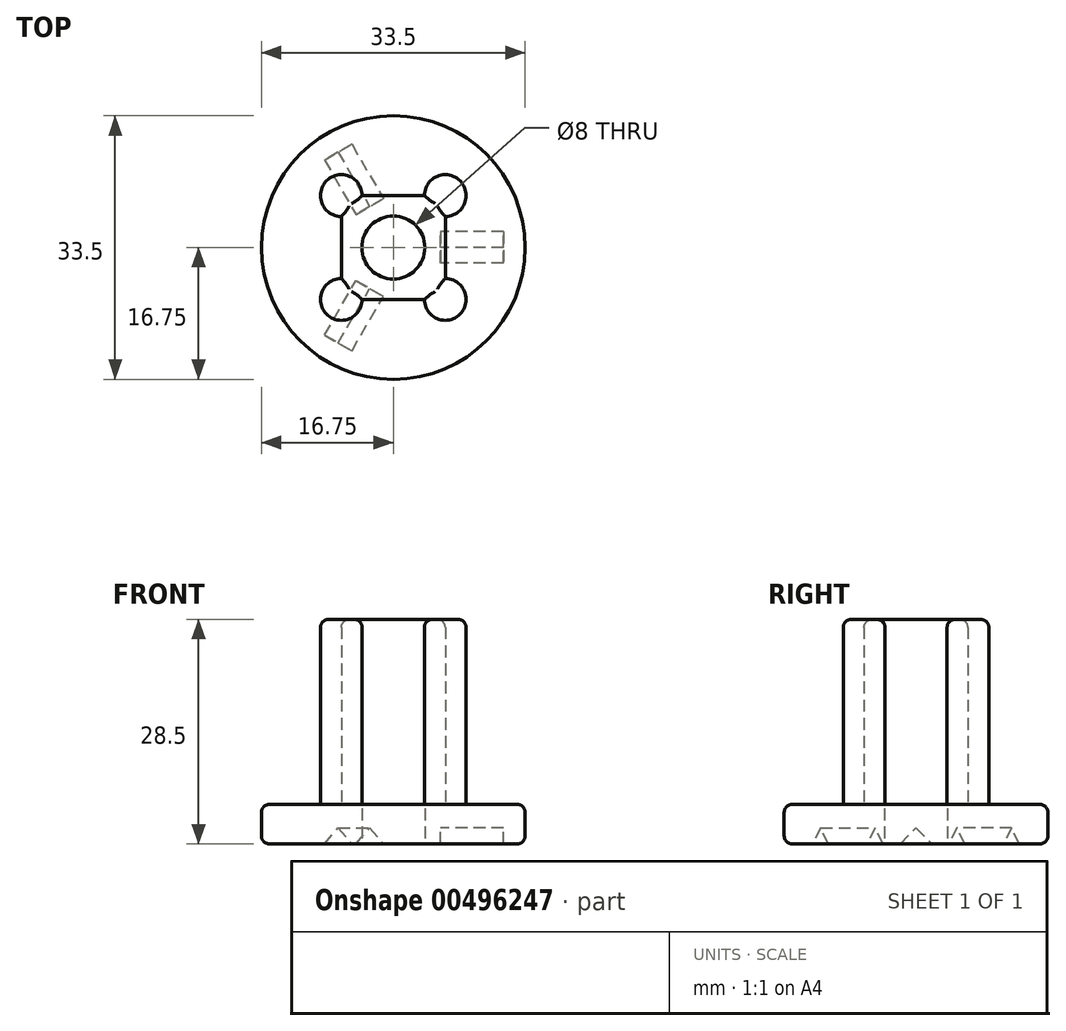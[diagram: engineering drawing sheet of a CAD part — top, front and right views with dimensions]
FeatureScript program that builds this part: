
annotation { "Feature Type Name" : "Feature", "Feature Type Description" : "" }
export const myFeature = defineFeature(function(context is Context, id is Id, definition is map)
    precondition{}
    {
        {
            var Q0;
            Q0=qCreatedBy(makeId("Top.planeOp"),FACE);
            var sketch = newSketch(context, id + "F0", { "sketchPlane" : qUnion([Q0])});
            skCircle(sketch, "E0", {"center": v(0, 0) * mm, "radius": 16.75 * mm});
            skSolve(sketch);
        }
        {
            var Q0;
            Q0=makeQuery(id+"F0.imprint","IMPRINT",FACE,{"disambiguationData":[TD([[makeQuery(id+"F0.imprint","IMPRINT",EDGE,{"derivedFrom":sQuery(id+"F0.wireOp",EDGE,"E0")}),1.0]])]});
            extrude(context, id + "F1", {"entities" : qUnion([Q0]), "depth" : 5 * mm});
        }
        {
            var Q0;
            Q0=makeQuery(id+"F1.opExtrude","CAP_FACE",FACE,{"disambiguationData":[OSD([sQuery(id+"F0.wireOp",EDGE,"E0")])],"isStart":false});
            var sketch = newSketch(context, id + "F2", { "sketchPlane" : qUnion([Q0])});
            skLineSegment(sketch, "E1.bottom", {"start": v(-3.95, 6.6) * mm, "end": v(3.95, 6.6) * mm});
            skLineSegment(sketch, "E1.top", {"start": v(-3.95, -6.6) * mm, "end": v(3.95, -6.6) * mm});
            skLineSegment(sketch, "E1.left", {"start": v(-6.6, 3.95) * mm, "end": v(-6.6, -3.95) * mm});
            skLineSegment(sketch, "E1.right", {"start": v(6.6, 3.95) * mm, "end": v(6.6, -3.95) * mm});
            skArc(sketch, "E2", {"start": v(-3.95, 6.6) * mm, "mid": v(-8.47, 8.47) * mm, "end": v(-6.6, 3.95) * mm});
            skArc(sketch, "E3", {"start": v(6.6, 3.95) * mm, "mid": v(8.47, 8.47) * mm, "end": v(3.95, 6.6) * mm});
            skArc(sketch, "E4", {"start": v(-6.6, -3.95) * mm, "mid": v(-8.47, -8.47) * mm, "end": v(-3.95, -6.6) * mm});
            skArc(sketch, "E5", {"start": v(3.95, -6.6) * mm, "mid": v(8.47, -8.47) * mm, "end": v(6.6, -3.95) * mm});
            skSolve(sketch);
        }
        {
            var Q0;
            Q0=makeQuery(id+"F2.imprint","IMPRINT",FACE,{"disambiguationData":[TD([[makeQuery(id+"F2.imprint","IMPRINT",EDGE,{"derivedFrom":sQuery(id+"F2.wireOp",EDGE,"E1.bottom")}),-1.0]])]});
            extrude(context, id + "F3", {"entities" : qUnion([Q0]), "operationType" : NewBodyOperationType.ADD, "depth" : 23.5 * mm});
        }
        {
            var Q0;
            Q0=makeQuery(id+"F1.opExtrude","CAP_FACE",FACE,{"disambiguationData":[OSD([sQuery(id+"F0.wireOp",EDGE,"E0")])],"isStart":true});
            var sketch = newSketch(context, id + "F4", { "sketchPlane" : qUnion([Q0])});
            skCircle(sketch, "E6", {"center": v(0, 0) * mm, "radius": 4 * mm});
            skSolve(sketch);
        }
        {
            var Q0;
            Q0=makeQuery(id+"F4.imprint","IMPRINT",FACE,{"disambiguationData":[TD([[makeQuery(id+"F4.imprint","IMPRINT",EDGE,{"derivedFrom":sQuery(id+"F4.wireOp",EDGE,"E6")}),1.0]])]});
            extrude(context, id + "F5", {"entities" : qUnion([Q0]), "operationType" : NewBodyOperationType.REMOVE, "endBound" : BoundingType.THROUGH_ALL, "oppositeDirection" : true, "depth" : 25 * mm});
        }
        {
            var Q0;
            Q0=qCreatedBy(makeId("Right.planeOp"),FACE);
            var sketch = newSketch(context, id + "F6", { "sketchPlane" : qUnion([Q0])});
            skLineSegment(sketch, "E7", {"start": v(-2, 0) * mm, "end": v(0, 2) * mm});
            skLineSegment(sketch, "E8", {"start": v(0, 2) * mm, "end": v(2, 0) * mm});
            skLineSegment(sketch, "E9", {"start": v(2, 0) * mm, "end": v(-2, 0) * mm});
            skSolve(sketch);
        }
        {
            var Q0;
            Q0=makeQuery(id+"F6.imprint","IMPRINT",FACE,{"disambiguationData":[TD([[makeQuery(id+"F6.imprint","IMPRINT",EDGE,{"derivedFrom":sQuery(id+"F6.wireOp",EDGE,"E7")}),-1.0]])]});
            extrude(context, id + "F7", {"entities" : qUnion([Q0]), "depth" : 14 * mm, "hasSecondDirection" : true, "secondDirectionOppositeDirection" : false, "secondDirectionDepth" : 6 * mm});
        }
        {
            var Q0;
            Q0=qCreatedBy(makeId("Front.planeOp"),FACE);
            var sketch = newSketch(context, id + "F8", { "sketchPlane" : qUnion([Q0])});
            skLineSegment(sketch, "E10", {"start": v(0, -62.92) * mm, "end": v(0, 62.63) * mm, "construction": true});
            skSolve(sketch);
        }
        {
            var Q0;
            Q0=makeQuery(id+"F7.opExtrude","SWEPT_BODY",BODY,{"disambiguationData":[OSD([sQuery(id+"F6.wireOp",EDGE,"E7"),sQuery(id+"F6.wireOp",EDGE,"E8"),sQuery(id+"F6.wireOp",EDGE,"E9")])]});
            var Q1;
            Q1=sQuery(id+"F8.wireOp",EDGE,"E10");
            circularPattern(context, id + "F9", {"entities" : qUnion([Q0]), "axis" : qUnion([Q1]), "angle" : 360 * degree, "instanceCount" : 3, "equalSpace" : true});
        }
        {
            var Q0;
            Q0=makeQuery(id+"F7.opExtrude","SWEPT_BODY",BODY,{"disambiguationData":[OSD([sQuery(id+"F6.wireOp",EDGE,"E7"),sQuery(id+"F6.wireOp",EDGE,"E8"),sQuery(id+"F6.wireOp",EDGE,"E9")])]});
            var Q1;
            Q1=makeQuery(id+"F9.opPattern","COPY",BODY,{"derivedFrom":makeQuery(id+"F7.opExtrude","SWEPT_BODY",BODY,{"disambiguationData":[OSD([sQuery(id+"F6.wireOp",EDGE,"E7"),sQuery(id+"F6.wireOp",EDGE,"E8"),sQuery(id+"F6.wireOp",EDGE,"E9")])]}),"instanceName":"1"});
            var Q2;
            Q2=makeQuery(id+"F9.opPattern","COPY",BODY,{"derivedFrom":makeQuery(id+"F7.opExtrude","SWEPT_BODY",BODY,{"disambiguationData":[OSD([sQuery(id+"F6.wireOp",EDGE,"E7"),sQuery(id+"F6.wireOp",EDGE,"E8"),sQuery(id+"F6.wireOp",EDGE,"E9")])]}),"instanceName":"2"});
            var Q3;
            Q3=makeQuery(id+"F1.opExtrude","SWEPT_BODY",BODY,{"disambiguationData":[OSD([sQuery(id+"F0.wireOp",EDGE,"E0")])]});
            booleanBodies(context, id + "F10", {"operationType" : BooleanOperationType.SUBTRACTION, "tools" : qUnion([Q0, Q1, Q2]), "targets" : qUnion([Q3])});
        }
        {
            var Q0;
            Q0=makeQuery(id+"F1.opExtrude","CAP_EDGE",EDGE,{"disambiguationData":[OSD([sQuery(id+"F0.wireOp",EDGE,"E0")])],"isStart":true});
            var Q1;
            Q1=makeQuery(id+"F1.opExtrude","CAP_EDGE",EDGE,{"disambiguationData":[OSD([sQuery(id+"F0.wireOp",EDGE,"E0")])],"isStart":false});
            var Q2;
            Q2=makeQuery(id+"F3.opExtrude","CAP_EDGE",EDGE,{"disambiguationData":[OSD([sQuery(id+"F2.wireOp",EDGE,"E1.bottom")])],"isStart":false});
            var Q3;
            Q3=makeQuery(id+"F3.opExtrude","CAP_EDGE",EDGE,{"disambiguationData":[OSD([sQuery(id+"F2.wireOp",EDGE,"E2")])],"isStart":false});
            var Q4;
            Q4=makeQuery(id+"F3.opExtrude","CAP_EDGE",EDGE,{"disambiguationData":[OSD([sQuery(id+"F2.wireOp",EDGE,"E1.left")])],"isStart":false});
            var Q5;
            Q5=makeQuery(id+"F3.opExtrude","CAP_EDGE",EDGE,{"disambiguationData":[OSD([sQuery(id+"F2.wireOp",EDGE,"E4")])],"isStart":false});
            var Q6;
            Q6=makeQuery(id+"F3.opExtrude","CAP_EDGE",EDGE,{"disambiguationData":[OSD([sQuery(id+"F2.wireOp",EDGE,"E1.top")])],"isStart":false});
            var Q7;
            Q7=makeQuery(id+"F3.opExtrude","CAP_EDGE",EDGE,{"disambiguationData":[OSD([sQuery(id+"F2.wireOp",EDGE,"E5")])],"isStart":false});
            var Q8;
            Q8=makeQuery(id+"F3.opExtrude","CAP_EDGE",EDGE,{"disambiguationData":[OSD([sQuery(id+"F2.wireOp",EDGE,"E1.right")])],"isStart":false});
            var Q9;
            Q9=makeQuery(id+"F3.opExtrude","CAP_EDGE",EDGE,{"disambiguationData":[OSD([sQuery(id+"F2.wireOp",EDGE,"E3")])],"isStart":false});
            var Q10;
            Q10=makeQuery(id+"F5.boolean.opBoolean","COPY",EDGE,{"derivedFrom":makeQuery(id+"F5.opExtrude","CAP_EDGE",EDGE,{"disambiguationData":[OSD([sQuery(id+"F4.wireOp",EDGE,"E6")])],"isStart":true})});
            var Q11;
            Q11=makeQuery(id+"F5.boolean.opBoolean","INTERSECT",EDGE,{"derivedFrom":[makeQuery(id+"F3.opExtrude","CAP_FACE",FACE,{"disambiguationData":[OSD([sQuery(id+"F2.wireOp",EDGE,"E1.bottom"),sQuery(id+"F2.wireOp",EDGE,"E1.top"),sQuery(id+"F2.wireOp",EDGE,"E1.left"),sQuery(id+"F2.wireOp",EDGE,"E1.right"),sQuery(id+"F2.wireOp",EDGE,"E2"),sQuery(id+"F2.wireOp",EDGE,"E3"),sQuery(id+"F2.wireOp",EDGE,"E4"),sQuery(id+"F2.wireOp",EDGE,"E5")])],"isStart":false}),makeQuery(id+"F5.opExtrude","SWEPT_FACE",FACE,{"disambiguationData":[OSD([sQuery(id+"F4.wireOp",EDGE,"E6")])]})]});
            fillet(context, id + "F11", {"entities" : qUnion([Q0, Q1, Q2, Q3, Q4, Q5, Q6, Q7, Q8, Q9, Q10, Q11]), "radius" : 1 * mm, "tangentPropagation" : true, "allowEdgeOverflow" : false});
        }
    });
